FCSTD DOCUMENT
Label: lid
objects: Sketcher::SketchObject×1
note: 1 computed .brp shape members not serialized (recipe doc carries the construction recipe); baked Part::Feature solids carry a one-line shape summary decoded from their .brp

FEATURE [Sketcher::SketchObject] Sketch
  sketch-geometry (10):
    g0: LineSegment StartX=-166.614 StartY=135.81 StartZ=0 EndX=-166.614 EndY=4.8097 EndZ=0
    g1: LineSegment StartX=-157.614 StartY=-4.1903 StartZ=0 EndX=92.3855 EndY=-4.1903 EndZ=0
    g2: LineSegment StartX=101.386 StartY=4.8097 StartZ=0 EndX=101.386 EndY=135.81 EndZ=0
    g3: LineSegment StartX=101.386 StartY=135.81 StartZ=0 EndX=-166.614 EndY=135.81 EndZ=0
    g4: ArcOfCircle CenterX=-157.614 CenterY=4.8097 CenterZ=0 NormalX=0 NormalY=0 NormalZ=1 Radius=9 StartAngle=3.14159 EndAngle=4.71239
    g5: ArcOfCircle CenterX=92.3855 CenterY=4.8097 CenterZ=0 NormalX=0 NormalY=0 NormalZ=1 Radius=9 StartAngle=4.71239 EndAngle=6.28319
    g6: Circle CenterX=-103.114 CenterY=128.31 CenterZ=0 NormalX=0 NormalY=0 NormalZ=1 Radius=1.75
    g7: Circle CenterX=-93.1145 CenterY=128.31 CenterZ=0 NormalX=0 NormalY=0 NormalZ=1 Radius=1.75
    g8: Circle CenterX=27.8855 CenterY=128.31 CenterZ=0 NormalX=0 NormalY=0 NormalZ=1 Radius=1.75
    g9: Circle CenterX=37.8855 CenterY=128.31 CenterZ=0 NormalX=0 NormalY=0 NormalZ=1 Radius=1.75
  constraints (28):
    c: Vertical(g0)
    c: Horizontal(g1)
    c: Coincident(g2,g3)
    c: Horizontal(g3)
    c: Tangent(g1,g4)
    c: Tangent(g0,g4)
    c: Tangent(g2,g5)
    c: Tangent(g1,g5)
    c: Vertical(g2)
    c: Coincident(g3,g0)
    c: DistanceY(g0,g2) = 0
    c: DistanceX(g1,g2) = 9
    c: DistanceY(g0,g0) = 131
    c: DistanceX(g2) = 101.386
    c: DistanceY(g2) = 135.81
    c: Radius(g8) = 1.75
    c: Radius(g9) = 1.75
    c: Radius(g7) = 1.75
    c: Radius(g6) = 1.75
    c: DistanceY(g6,g7) = 0
    c: DistanceY(g7,g8) = 0
    c: DistanceY(g8,g9) = 0
    c: DistanceY(g0,g6) = -7.5
    c: DistanceX(g6,g7) = 10
    c: DistanceX(g8,g9) = 10
    c: DistanceX(g0,g2) = 268
    c: DistanceX(g0,g6) = 63.5
    c: DistanceX(g9,g2) = 63.5
